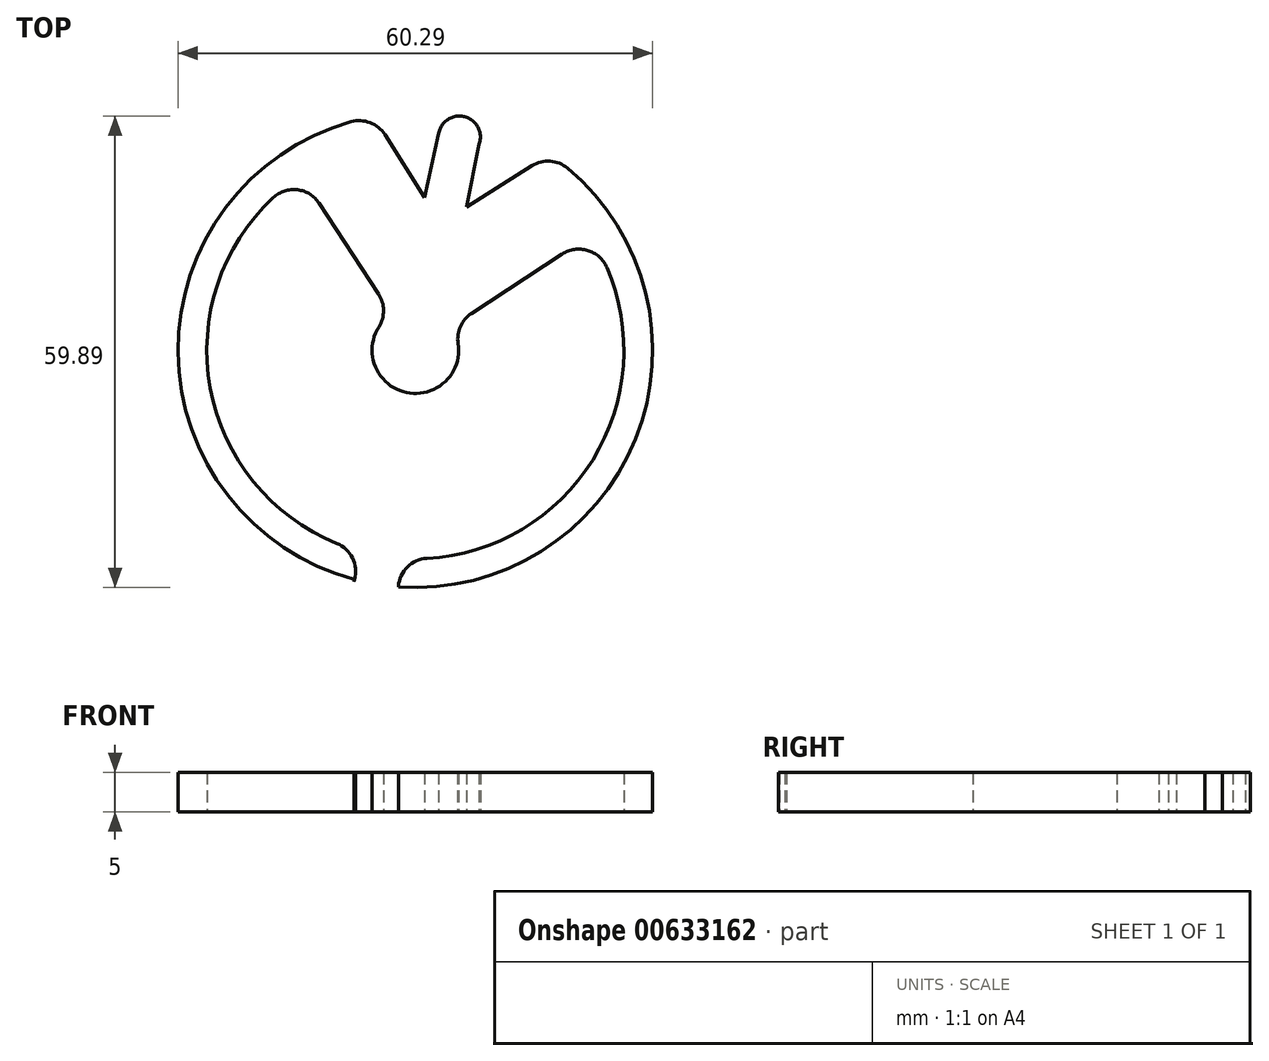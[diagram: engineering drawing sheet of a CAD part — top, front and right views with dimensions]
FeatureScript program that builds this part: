
annotation { "Feature Type Name" : "Feature", "Feature Type Description" : "" }
export const myFeature = defineFeature(function(context is Context, id is Id, definition is map)
    precondition{}
    {
        {
            var Q0;
            Q0=qCreatedBy(makeId("Top.planeOp"),FACE);
            var sketch = newSketch(context, id + "F0", { "sketchPlane" : qUnion([Q0])});
            skArc(sketch, "E0", {"start": v(-163.39, 46.5) * mm, "mid": v(-133.28, 65.26) * mm, "end": v(-141.88, 99.67) * mm});
            skArc(sketch, "E1", {"start": v(-179.3, 95.93) * mm, "mid": v(-187.28, 71.76) * mm, "end": v(-171.21, 52.03) * mm});
            skArc(sketch, "E2", {"start": v(-165.87, 79.51) * mm, "mid": v(-162.35, 71.18) * mm, "end": v(-155.8, 77.4) * mm});
            skLineSegment(sketch, "E3", {"start": v(-154.1, 81.23) * mm, "end": v(-142.57, 88.77) * mm});
            skLineSegment(sketch, "E4", {"start": v(-165.9, 83.7) * mm, "end": v(-173.44, 95.22) * mm});
            skLineSegment(sketch, "E5.trimOffspring", {"start": v(-163.38, 46.54) * mm, "end": v(-163.39, 46.5) * mm});
            skLineSegment(sketch, "E6.trimOffspring", {"start": v(-168.94, 47.42) * mm, "end": v(-169.02, 47.2) * mm});
            skArc(sketch, "E7.trimOffspring", {"start": v(-159.75, 50.11) * mm, "mid": v(-138.7, 62.64) * mm, "end": v(-136.92, 87.07) * mm});
            skArc(sketch, "E8.filletArc", {"start": v(-136.92, 87.07) * mm, "mid": v(-139.35, 89.24) * mm, "end": v(-142.57, 88.77) * mm});
            skArc(sketch, "E9.filletArc", {"start": v(-173.44, 95.22) * mm, "mid": v(-176.2, 96.94) * mm, "end": v(-179.3, 95.93) * mm});
            skArc(sketch, "E10.filletArc", {"start": v(-154.1, 81.23) * mm, "mid": v(-155.5, 79.57) * mm, "end": v(-155.8, 77.4) * mm});
            skArc(sketch, "E11.filletArc", {"start": v(-165.87, 79.51) * mm, "mid": v(-165.27, 81.6) * mm, "end": v(-165.9, 83.7) * mm});
            skLineSegment(sketch, "E12", {"start": v(-165.1, 103.92) * mm, "end": v(-160.07, 95.93) * mm});
            skLineSegment(sketch, "E13", {"start": v(-154.75, 94.73) * mm, "end": v(-146.41, 99.98) * mm});
            skArc(sketch, "E14.trimOffspring", {"start": v(-169.41, 105.57) * mm, "mid": v(-191.37, 76.32) * mm, "end": v(-168.94, 47.42) * mm});
            skArc(sketch, "E15.filletArc", {"start": v(-165.1, 103.92) * mm, "mid": v(-166.98, 105.46) * mm, "end": v(-169.41, 105.57) * mm});
            skArc(sketch, "E16.filletArc", {"start": v(-141.88, 99.67) * mm, "mid": v(-144.1, 100.56) * mm, "end": v(-146.41, 99.98) * mm});
            skArc(sketch, "E17.filletArc", {"start": v(-159.75, 50.11) * mm, "mid": v(-162.24, 49) * mm, "end": v(-163.38, 46.54) * mm});
            skArc(sketch, "E18.filletArc", {"start": v(-169.02, 47.2) * mm, "mid": v(-169.16, 50.05) * mm, "end": v(-171.21, 52.03) * mm});
            skArc(sketch, "E19", {"start": v(-168.29, 105.72) * mm, "mid": v(-191.23, 76.88) * mm, "end": v(-168.92, 47.56) * mm});
            skLineSegment(sketch, "E20", {"start": v(-154.75, 94.73) * mm, "end": v(-153.04, 103.15) * mm});
            skLineSegment(sketch, "E21", {"start": v(-160.07, 95.93) * mm, "end": v(-158.21, 104.32) * mm});
            skArc(sketch, "E22", {"start": v(-153.12, 102.75) * mm, "mid": v(-154.96, 106.21) * mm, "end": v(-158.26, 104.1) * mm});
            skArc(sketch, "E23.trimOffspring", {"start": v(-163.37, 46.64) * mm, "mid": v(-133.21, 65.83) * mm, "end": v(-142.84, 100.27) * mm});
            skSolve(sketch);
        }
        {
            var Q0;
            Q0 = qSketchRegion(id + "F0", true);
            extrude(context, id + "F1", {"entities" : qUnion([Q0]), "depth" : 5 * mm, "offsetDistance" : 25 * mm});
        }
    });
